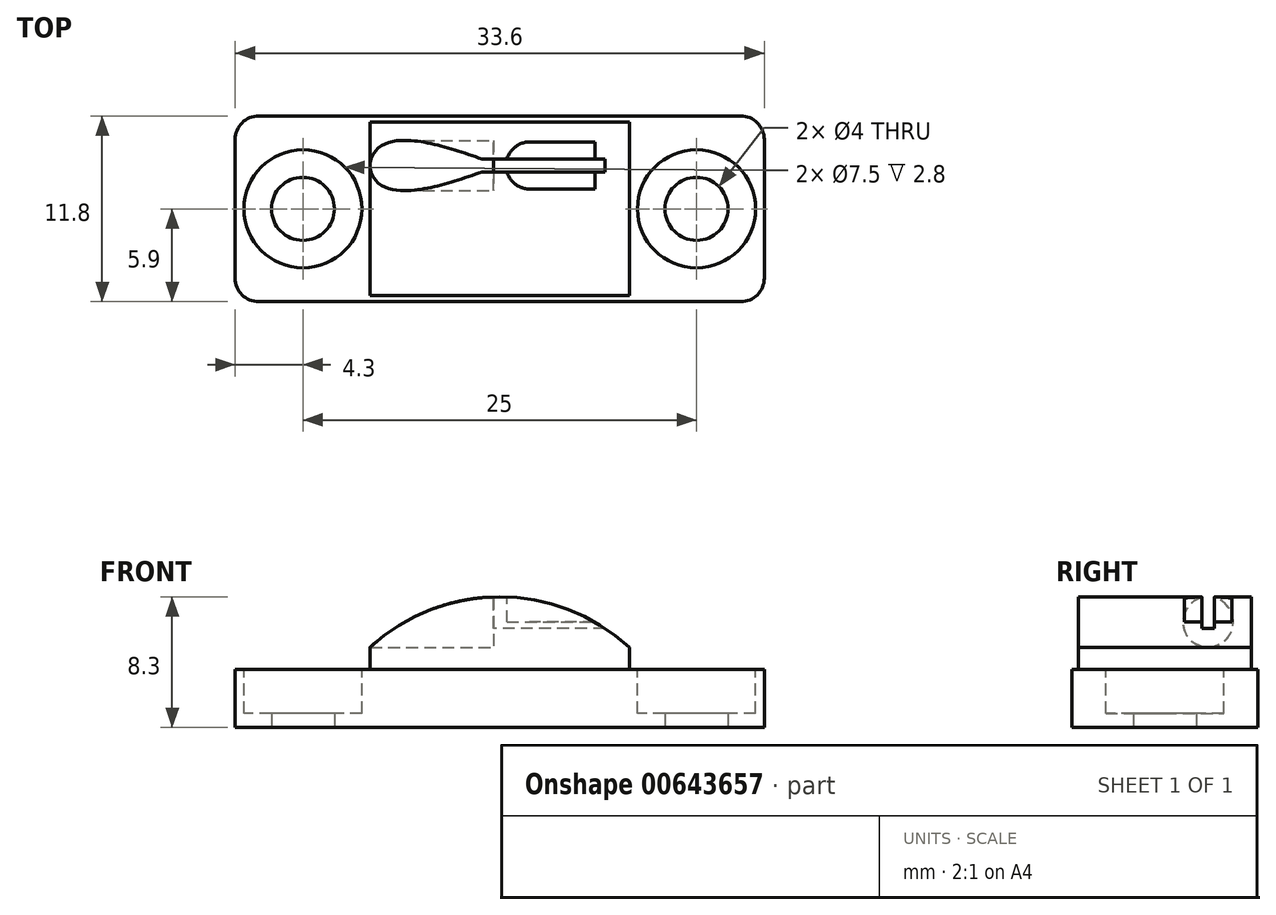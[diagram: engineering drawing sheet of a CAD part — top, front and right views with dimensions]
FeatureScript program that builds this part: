
annotation { "Feature Type Name" : "Feature", "Feature Type Description" : "" }
export const myFeature = defineFeature(function(context is Context, id is Id, definition is map)
    precondition{}
    {
        {
            var Q0;
            Q0=qCreatedBy(makeId("Top.planeOp"),FACE);
            var sketch = newSketch(context, id + "F0", { "sketchPlane" : qUnion([Q0])});
            skLineSegment(sketch, "E0.bottom", {"start": v(-16.8, 5.9) * mm, "end": v(16.8, 5.9) * mm});
            skLineSegment(sketch, "E0.top", {"start": v(-16.8, -5.9) * mm, "end": v(16.8, -5.9) * mm});
            skLineSegment(sketch, "E0.left", {"start": v(-16.8, 5.9) * mm, "end": v(-16.8, -5.9) * mm});
            skLineSegment(sketch, "E0.right", {"start": v(16.8, 5.9) * mm, "end": v(16.8, -5.9) * mm});
            skPoint(sketch, "E0.middle", {"position": v(0, 0) * mm});
            skCircle(sketch, "E1", {"center": v(-12.5, 0) * mm, "radius": 2 * mm});
            skCircle(sketch, "E2", {"center": v(12.5, 0) * mm, "radius": 2 * mm});
            skSolve(sketch);
        }
        {
            var Q0;
            Q0 = qSketchRegion(id + "F0", true);
            extrude(context, id + "F1", {"entities" : qUnion([Q0]), "depth" : 3.7 * mm, "offsetDistance" : 25 * mm});
        }
        {
            var Q0;
            Q0=makeQuery(id+"F1.opExtrude","CAP_FACE",FACE,{"disambiguationData":[OSD([sQuery(id+"F0.wireOp",EDGE,"E0.bottom"),sQuery(id+"F0.wireOp",EDGE,"E0.top"),sQuery(id+"F0.wireOp",EDGE,"E0.left"),sQuery(id+"F0.wireOp",EDGE,"E0.right"),sQuery(id+"F0.wireOp",EDGE,"E1"),sQuery(id+"F0.wireOp",EDGE,"E2")])],"isStart":false});
            var sketch = newSketch(context, id + "F2", { "sketchPlane" : qUnion([Q0])});
            skCircle(sketch, "E3", {"center": v(-12.5, 0) * mm, "radius": 3.75 * mm});
            skCircle(sketch, "E4", {"center": v(12.5, 0) * mm, "radius": 3.75 * mm});
            skSolve(sketch);
        }
        {
            var Q0;
            Q0=makeQuery(id+"F2.imprint","IMPRINT",FACE,{"disambiguationData":[TD([[makeQuery(id+"F2.imprint","IMPRINT",EDGE,{"derivedFrom":sQuery(id+"F2.wireOp",EDGE,"E3")}),1.0]])]});
            var Q1;
            Q1=makeQuery(id+"F2.imprint","IMPRINT",FACE,{"disambiguationData":[TD([[makeQuery(id+"F2.imprint","IMPRINT",EDGE,{"derivedFrom":sQuery(id+"F2.wireOp",EDGE,"E4")}),1.0]])]});
            extrude(context, id + "F3", {"entities" : qUnion([Q0, Q1]), "operationType" : NewBodyOperationType.REMOVE, "oppositeDirection" : true, "depth" : 2.8 * mm, "offsetDistance" : 25 * mm});
        }
        {
            var Q0;
            Q0=qCreatedBy(makeId("Front.planeOp"),FACE);
            var sketch = newSketch(context, id + "F4", { "sketchPlane" : qUnion([Q0])});
            skLineSegment(sketch, "E5", {"start": v(-8.24, 5.1) * mm, "end": v(-8.25, 3.7) * mm});
            skLineSegment(sketch, "E6", {"start": v(8.24, 5.1) * mm, "end": v(8.25, 3.7) * mm});
            skArc(sketch, "E7", {"start": v(8.24, 5.1) * mm, "mid": v(0, 8.3) * mm, "end": v(-8.24, 5.1) * mm});
            skLineSegment(sketch, "E8", {"start": v(-8.25, 3.7) * mm, "end": v(8.25, 3.7) * mm});
            skSolve(sketch);
        }
        {
            var Q0;
            Q0 = qSketchRegion(id + "F4", true);
            extrude(context, id + "F5", {"entities" : qUnion([Q0]), "operationType" : NewBodyOperationType.ADD, "endBound" : BoundingType.SYMMETRIC, "depth" : 11 * mm, "offsetDistance" : 25 * mm});
        }
        {
            var Q0;
            Q0=qCreatedBy(makeId("Right.planeOp"),FACE);
            var sketch = newSketch(context, id + "F6", { "sketchPlane" : qUnion([Q0])});
            skCircle(sketch, "E9", {"center": v(2.75, 6.7) * mm, "radius": 1.6 * mm});
            skLineSegment(sketch, "E10", {"start": v(5.5, 8.3) * mm, "end": v(0.73, 8.3) * mm, "construction": true});
            skLineSegment(sketch, "E11", {"start": v(2.75, 6.7) * mm, "end": v(0, 6.7) * mm, "construction": true});
            skLineSegment(sketch, "E12", {"start": v(2.75, 6.7) * mm, "end": v(5.5, 6.7) * mm, "construction": true});
            skSolve(sketch);
        }
        {
            var Q0;
            Q0 = qSketchRegion(id + "F6", true);
            extrude(context, id + "F7", {"entities" : qUnion([Q0]), "operationType" : NewBodyOperationType.REMOVE, "endBound" : BoundingType.THROUGH_ALL, "oppositeDirection" : true, "depth" : 25 * mm, "offsetDistance" : 25 * mm, "hasSecondDirection" : true, "secondDirectionOppositeDirection" : true, "secondDirectionDepth" : 0.4 * mm});
        }
        {
            var Q0;
            Q0=makeQuery(id+"F7.boolean.opBoolean","COPY",FACE,{"derivedFrom":makeQuery(id+"F7.opExtrude","CAP_FACE",FACE,{"disambiguationData":[OSD([sQuery(id+"F6.wireOp",EDGE,"E9")])],"isStart":true})});
            var sketch = newSketch(context, id + "F8", { "sketchPlane" : qUnion([Q0])});
            skLineSegment(sketch, "E13.bottom", {"start": v(-3.15, 8.3) * mm, "end": v(-2.35, 8.3) * mm});
            skLineSegment(sketch, "E13.top", {"start": v(-3.15, 6.3) * mm, "end": v(-2.35, 6.3) * mm});
            skLineSegment(sketch, "E13.left", {"start": v(-3.15, 8.3) * mm, "end": v(-3.15, 6.3) * mm});
            skLineSegment(sketch, "E13.right", {"start": v(-2.35, 8.3) * mm, "end": v(-2.35, 6.3) * mm});
            skPoint(sketch, "E13.middle", {"position": v(-2.75, 7.3) * mm});
            skLineSegment(sketch, "E14", {"start": v(-3.15, 8.3) * mm, "end": v(-5.5, 8.3) * mm, "construction": true});
            skLineSegment(sketch, "E15", {"start": v(-2.35, 8) * mm, "end": v(0, 8) * mm, "construction": true});
            skSolve(sketch);
        }
        {
            var Q0;
            Q0 = qSketchRegion(id + "F8", true);
            extrude(context, id + "F9", {"entities" : qUnion([Q0]), "operationType" : NewBodyOperationType.REMOVE, "endBound" : BoundingType.THROUGH_ALL, "oppositeDirection" : true, "depth" : 25 * mm, "offsetDistance" : 25 * mm, "hasSecondDirection" : true, "secondDirectionOppositeDirection" : false, "secondDirectionDepth" : 1 * mm});
        }
        {
            var Q0;
            Q0=makeQuery(id+"F5.opExtrude","CAP_EDGE",EDGE,{"disambiguationData":[OSD([sQuery(id+"F4.wireOp",EDGE,"E7")])],"isStart":false});
            cPoint(context, id + "F10", {"entities" : qUnion([Q0]), "parameter" : 0.5});
        }
        {
            var Q0;
            Q0=qCreatedBy(makeId("Top.planeOp"),FACE);
            var Q1;
            Q1 = qCreatedBy(id + "F10" ,VERTEX);
            cPlane(context, id + "F11", {"entities" : qUnion([Q0, Q1]), "cplaneType" : CPlaneType.PLANE_POINT, "offset" : 25 * mm, "width" : 150 * mm, "height" : 150 * mm});
        }
        {
            var Q0;
            Q0=qCreatedBy(id+"F11.planeOp",FACE);
            var sketch = newSketch(context, id + "F12", { "sketchPlane" : qUnion([Q0])});
            skArc(sketch, "E16", {"start": v(1.9, 4.25) * mm, "mid": v(0.4, 2.75) * mm, "end": v(1.9, 1.25) * mm});
            skLineSegment(sketch, "E17", {"start": v(1.9, 2.75) * mm, "end": v(1.9, 5.5) * mm, "construction": true});
            skLineSegment(sketch, "E18", {"start": v(1.9, 5.5) * mm, "end": v(0, 5.5) * mm, "construction": true});
            skLineSegment(sketch, "E19", {"start": v(0, 0) * mm, "end": v(1.9, 0) * mm, "construction": true});
            skLineSegment(sketch, "E20", {"start": v(1.9, 0) * mm, "end": v(1.9, 2.75) * mm, "construction": true});
            skLineSegment(sketch, "E21", {"start": v(1.9, 4.25) * mm, "end": v(8.24, 4.25) * mm});
            skLineSegment(sketch, "E22", {"start": v(8.24, 4.25) * mm, "end": v(8.24, 1.25) * mm});
            skLineSegment(sketch, "E23", {"start": v(8.24, 1.25) * mm, "end": v(1.9, 1.25) * mm});
            skSolve(sketch);
        }
        {
            var Q0;
            Q0 = qSketchRegion(id + "F12", true);
            extrude(context, id + "F13", {"entities" : qUnion([Q0]), "operationType" : NewBodyOperationType.REMOVE, "oppositeDirection" : true, "depth" : 1.6 * mm, "offsetDistance" : 25 * mm});
        }
        {
            var Q0;
            Q0=makeQuery(id+"F1.opExtrude","SWEPT_EDGE",EDGE,{"disambiguationData":[OSD([sQuery(id+"F0.wireOp",EDGE,"E0.top"),sQuery(id+"F0.wireOp",EDGE,"E0.left")])]});
            var Q1;
            Q1=makeQuery(id+"F1.opExtrude","SWEPT_EDGE",EDGE,{"disambiguationData":[OSD([sQuery(id+"F0.wireOp",EDGE,"E0.top"),sQuery(id+"F0.wireOp",EDGE,"E0.right")])]});
            var Q2;
            Q2=makeQuery(id+"F1.opExtrude","SWEPT_EDGE",EDGE,{"disambiguationData":[OSD([sQuery(id+"F0.wireOp",EDGE,"E0.bottom"),sQuery(id+"F0.wireOp",EDGE,"E0.right")])]});
            var Q3;
            Q3=makeQuery(id+"F1.opExtrude","SWEPT_EDGE",EDGE,{"disambiguationData":[OSD([sQuery(id+"F0.wireOp",EDGE,"E0.bottom"),sQuery(id+"F0.wireOp",EDGE,"E0.left")])]});
            fillet(context, id + "F14", {"entities" : qUnion([Q0, Q1, Q2, Q3]), "radius" : 1.5 * mm, "tangentPropagation" : true, "allowEdgeOverflow" : false});
        }
    });
